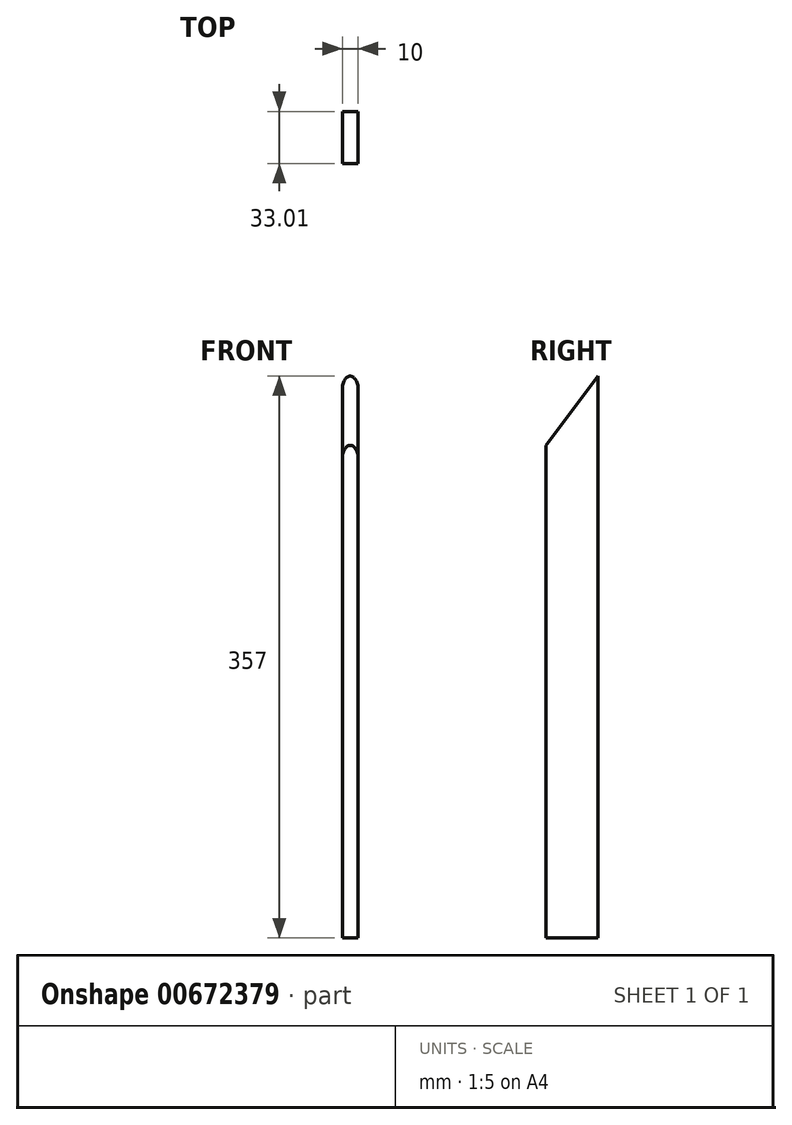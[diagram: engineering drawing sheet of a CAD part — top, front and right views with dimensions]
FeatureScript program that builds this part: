
annotation { "Feature Type Name" : "Feature", "Feature Type Description" : "" }
export const myFeature = defineFeature(function(context is Context, id is Id, definition is map)
    precondition{}
    {
        {
            var Q0;
            Q0=qCreatedBy(makeId("Right.planeOp"),FACE);
            var sketch = newSketch(context, id + "F0", { "sketchPlane" : qUnion([Q0])});
            skLineSegment(sketch, "E0.bottom", {"start": v(-56.57, 0) * mm, "end": v(-42.08, 0) * mm});
            skLineSegment(sketch, "E0.top", {"start": v(-56.57, 313) * mm, "end": v(-42.08, 313) * mm});
            skLineSegment(sketch, "E0.left", {"start": v(-56.57, 0) * mm, "end": v(-56.57, 313) * mm});
            skLineSegment(sketch, "E0.right", {"start": v(-42.08, 0) * mm, "end": v(-42.08, 313) * mm});
            skLineSegment(sketch, "E1", {"start": v(-23.56, 0) * mm, "end": v(-23.56, 357) * mm});
            skLineSegment(sketch, "E2", {"start": v(-23.56, 357) * mm, "end": v(-56.57, 313) * mm});
            skLineSegment(sketch, "E3", {"start": v(-42.08, 0) * mm, "end": v(-23.56, 0) * mm});
            skSolve(sketch);
        }
        {
            var Q0;
            Q0 = qSketchRegion(id + "F0", true);
            extrude(context, id + "F1", {"entities" : qUnion([Q0]), "depth" : 10 * mm, "offsetDistance" : 25 * mm});
        }
        {
            var Q0;
            Q0=makeQuery(id+"F1.opExtrude","CAP_EDGE",EDGE,{"disambiguationData":[OSD([sQuery(id+"F0.wireOp",EDGE,"E2")])],"isStart":false});
            var Q1;
            Q1=makeQuery(id+"F1.opExtrude","CAP_EDGE",EDGE,{"disambiguationData":[OSD([sQuery(id+"F0.wireOp",EDGE,"E2")])],"isStart":true});
            fillet(context, id + "F2", {"entities" : qUnion([Q0, Q1]), "radius" : 5 * mm, "tangentPropagation" : true, "allowEdgeOverflow" : false});
        }
    });
